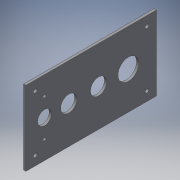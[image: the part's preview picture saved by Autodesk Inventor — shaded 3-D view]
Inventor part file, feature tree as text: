
AUTODESK INVENTOR PART (.ipt)
format: ipt  version: 2018 (Build 220112000, 112)  size: 153,600 bytes
history: native  units: in
note: dims shown in document units (in); Inventor stores cm internally (conversion verified against a paired STEP export)
features: extrude x4, sketch x4
ambient origin geometry x8: Origin, YZ Plane, XZ Plane, XY Plane, X Axis, Y Axis, Z Axis, Center Point
bodies: Solid1 (feature_tree)
feature tree (8):
  extrude  "Extrusion1"  Depth=7.0in
  extrude  "Extrusion2"  Depth=0.125in
  extrude  "Extrusion3"  Depth=0.875in
  extrude  "Extrusion4"  Depth=1.6in
  sketch  "Sketch1"  dims[d0=4.0in d1=7.0in]
  sketch  "Sketch2"  dims[d2=0.125in d3=0.0in d4=1.0in]
  sketch  "Sketch3"  dims[d5=1.3in d7=0.875in]
  sketch  "Sketch4"  dims[d8=1.6in d9=1.6in d10=0.875in d11=1.125in d12=0.5in d13=0.0in d14=0.75in d17=0.159in d18=0.159in d19=1.0in d20=0.0in d23=1.0in d24=0.5in d25=0.5in d26=0.5in d27=0.5in d28=0.5in d29=0.5in d30=0.5in d31=0.5in d32=0.2031in d33=0.2031in d34=0.2031in d35=0.2031in d36=1.0in d37=0.0in]
